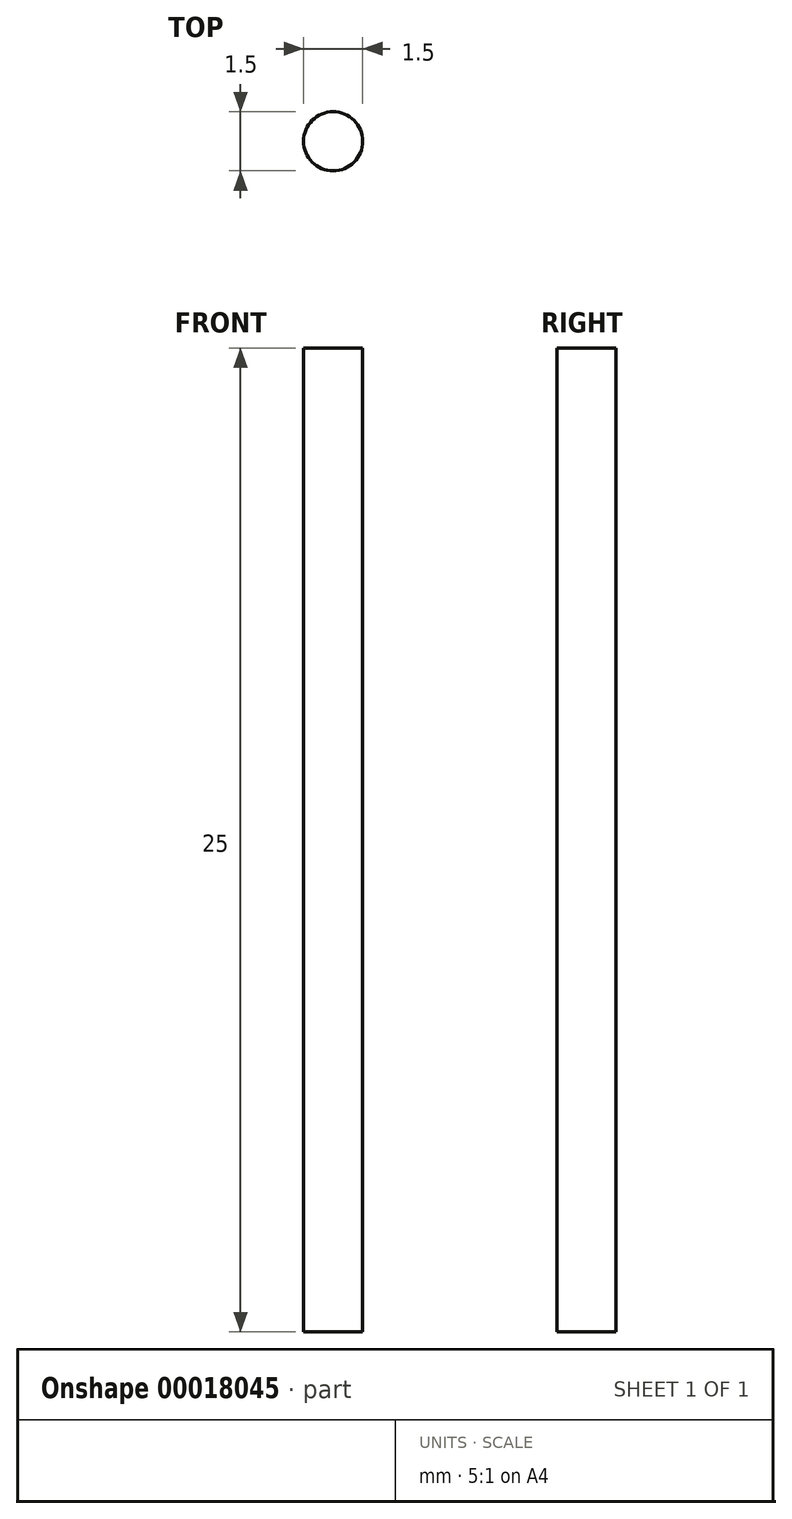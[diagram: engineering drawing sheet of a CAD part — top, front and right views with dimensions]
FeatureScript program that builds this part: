
annotation { "Feature Type Name" : "Feature", "Feature Type Description" : "" }
export const myFeature = defineFeature(function(context is Context, id is Id, definition is map)
    precondition{}
    {
        {
            var Q0;
            Q0=qCreatedBy(makeId("Top.planeOp"),FACE);
            var sketch = newSketch(context, id + "F0", { "sketchPlane" : qUnion([Q0])});
            skCircle(sketch, "E0", {"center": v(0, 0) * mm, "radius": 0.75 * mm});
            skSolve(sketch);
        }
        {
            var Q0;
            Q0 = qSketchRegion(id + "F0", true);
            extrude(context, id + "F1", {"entities" : qUnion([Q0]), "depth" : 25 * mm});
        }
    });
